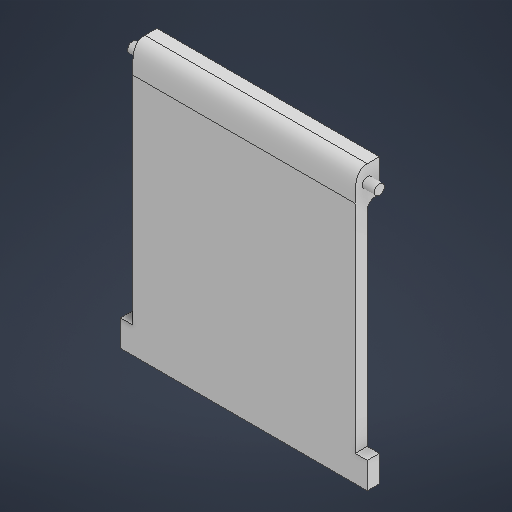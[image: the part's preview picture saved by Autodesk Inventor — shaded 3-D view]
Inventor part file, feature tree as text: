
AUTODESK INVENTOR PART (.ipt)
format: ipt  version: 2025.3 (Build 293356030, 356C)  size: 212,480 bytes
history: native  units: mm
features: extrude x4, sketch x4, other x1, fillet x1
ambient origin geometry x8: Origin, YZ Plane, XZ Plane, XY Plane, X Axis, Y Axis, Z Axis, Center Point
bodies: Body1 (feature_tree)
feature tree (10):
  other  "實體1"
  extrude  "擠出1"  Depth=61.0mm
  extrude  "擠出2"  Depth=55.0mm
  extrude  "擠出3"  Depth=6.5mm
  extrude  "擠出4"  Depth=60.5mm
  fillet  "圓角1"  Radius=3.0mm
  sketch  "草圖1"
  sketch  "草圖2"
  sketch  "草圖3"
  sketch  "草圖4"
